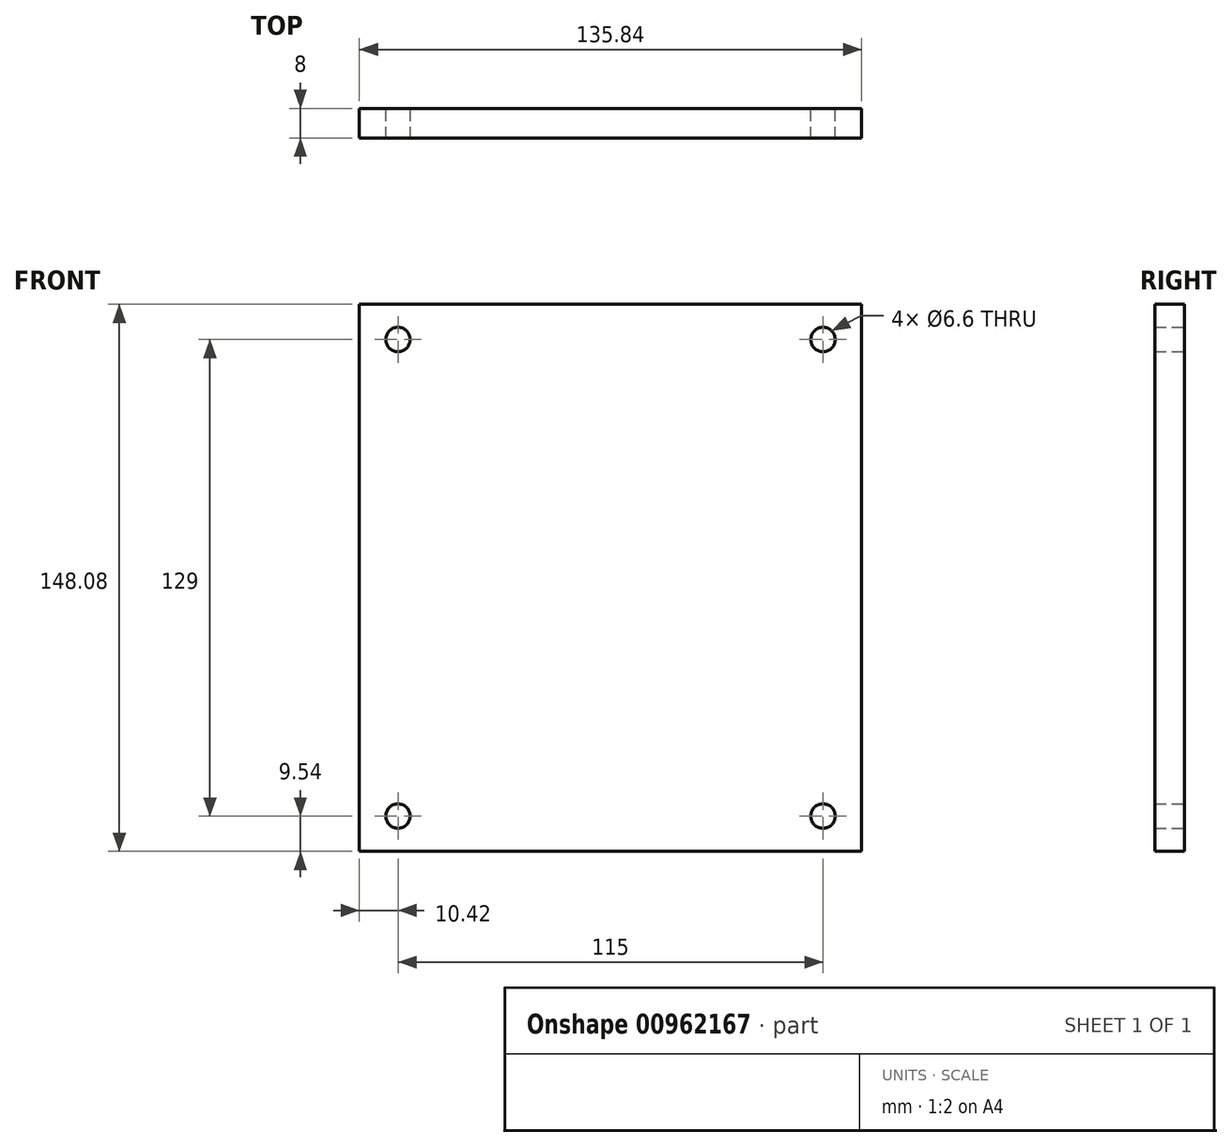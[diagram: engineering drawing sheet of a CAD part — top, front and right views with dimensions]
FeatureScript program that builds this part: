
annotation { "Feature Type Name" : "Feature", "Feature Type Description" : "" }
export const myFeature = defineFeature(function(context is Context, id is Id, definition is map)
    precondition{}
    {
        {
            var Q0;
            Q0=qCreatedBy(makeId("Front.planeOp"),FACE);
            var sketch = newSketch(context, id + "F0", { "sketchPlane" : qUnion([Q0])});
            skLineSegment(sketch, "E0.bottom", {"start": v(57.5, -64.5) * mm, "end": v(-57.5, -64.5) * mm});
            skLineSegment(sketch, "E0.top", {"start": v(57.5, 64.5) * mm, "end": v(-57.5, 64.5) * mm});
            skLineSegment(sketch, "E0.left", {"start": v(57.5, -64.5) * mm, "end": v(57.5, 64.5) * mm});
            skLineSegment(sketch, "E0.right", {"start": v(-57.5, -64.5) * mm, "end": v(-57.5, 64.5) * mm});
            skPoint(sketch, "E0.middle", {"position": v(0, 0) * mm});
            skLineSegment(sketch, "E1.bottom", {"start": v(67.92, 74.04) * mm, "end": v(-67.92, 74.04) * mm});
            skLineSegment(sketch, "E1.top", {"start": v(67.92, -74.04) * mm, "end": v(-67.92, -74.04) * mm});
            skLineSegment(sketch, "E1.left", {"start": v(67.92, 74.04) * mm, "end": v(67.92, -74.04) * mm});
            skLineSegment(sketch, "E1.right", {"start": v(-67.92, 74.04) * mm, "end": v(-67.92, -74.04) * mm});
            skSolve(sketch);
        }
        {
            var Q0;
            Q0=makeQuery(id+"F0.imprint","IMPRINT",FACE,{"disambiguationData":[TD([[makeQuery(id+"F0.imprint","IMPRINT",EDGE,{"derivedFrom":sQuery(id+"F0.wireOp",EDGE,"E0.bottom")}),1.0]])]});
            var Q1;
            Q1=makeQuery(id+"F0.imprint","IMPRINT",FACE,{"disambiguationData":[TD([[makeQuery(id+"F0.imprint","IMPRINT",EDGE,{"derivedFrom":sQuery(id+"F0.wireOp",EDGE,"E0.bottom")}),-1.0]])]});
            extrude(context, id + "F1", {"entities" : qUnion([Q0, Q1]), "depth" : 8 * mm, "offsetDistance" : 25 * mm});
        }
        {
            var Q0;
            Q0=sQuery(id+"F0.wireOp",VERTEX,"E0.top.end");
            var Q1;
            Q1=sQuery(id+"F0.wireOp",VERTEX,"E0.top.start");
            var Q2;
            Q2=sQuery(id+"F0.wireOp",VERTEX,"E0.bottom.start");
            var Q3;
            Q3=sQuery(id+"F0.wireOp",VERTEX,"E0.bottom.end");
            var Q4;
            Q4=makeQuery(id+"F1.opExtrude","SWEPT_BODY",BODY,{"disambiguationData":[OSD([sQuery(id+"F0.wireOp",EDGE,"E1.bottom"),sQuery(id+"F0.wireOp",EDGE,"E1.top"),sQuery(id+"F0.wireOp",EDGE,"E1.left"),sQuery(id+"F0.wireOp",EDGE,"E1.right")])]});
            hole(context, id + "F2", {"style" : HoleStyle.SIMPLE, "endStyle" : HoleEndStyle.THROUGH, "oppositeDirection" : true, "standardTappedOrClearance" : lookupTablePath({ "fit" : "Normal", "standard" : "ISO", "size" : "M6", "type" : "Clearance" }), "standardBlindInLast" : lookupTablePath({ "fit" : "Normal", "standard" : "ISO", "engagement" : "75%", "pitch" : "1 mm", "size" : "M6", "type" : "Clearance & tapped" }), "holeDiameter" : 6.6 * mm, "majorDiameter" : 6 * mm, "isTappedThrough" : true, "tappedDepth" : 12 * mm, "tapClearance" : 3, "locations" : qUnion([Q0, Q1, Q2, Q3]), "scope" : qUnion([Q4])});
        }
    });
